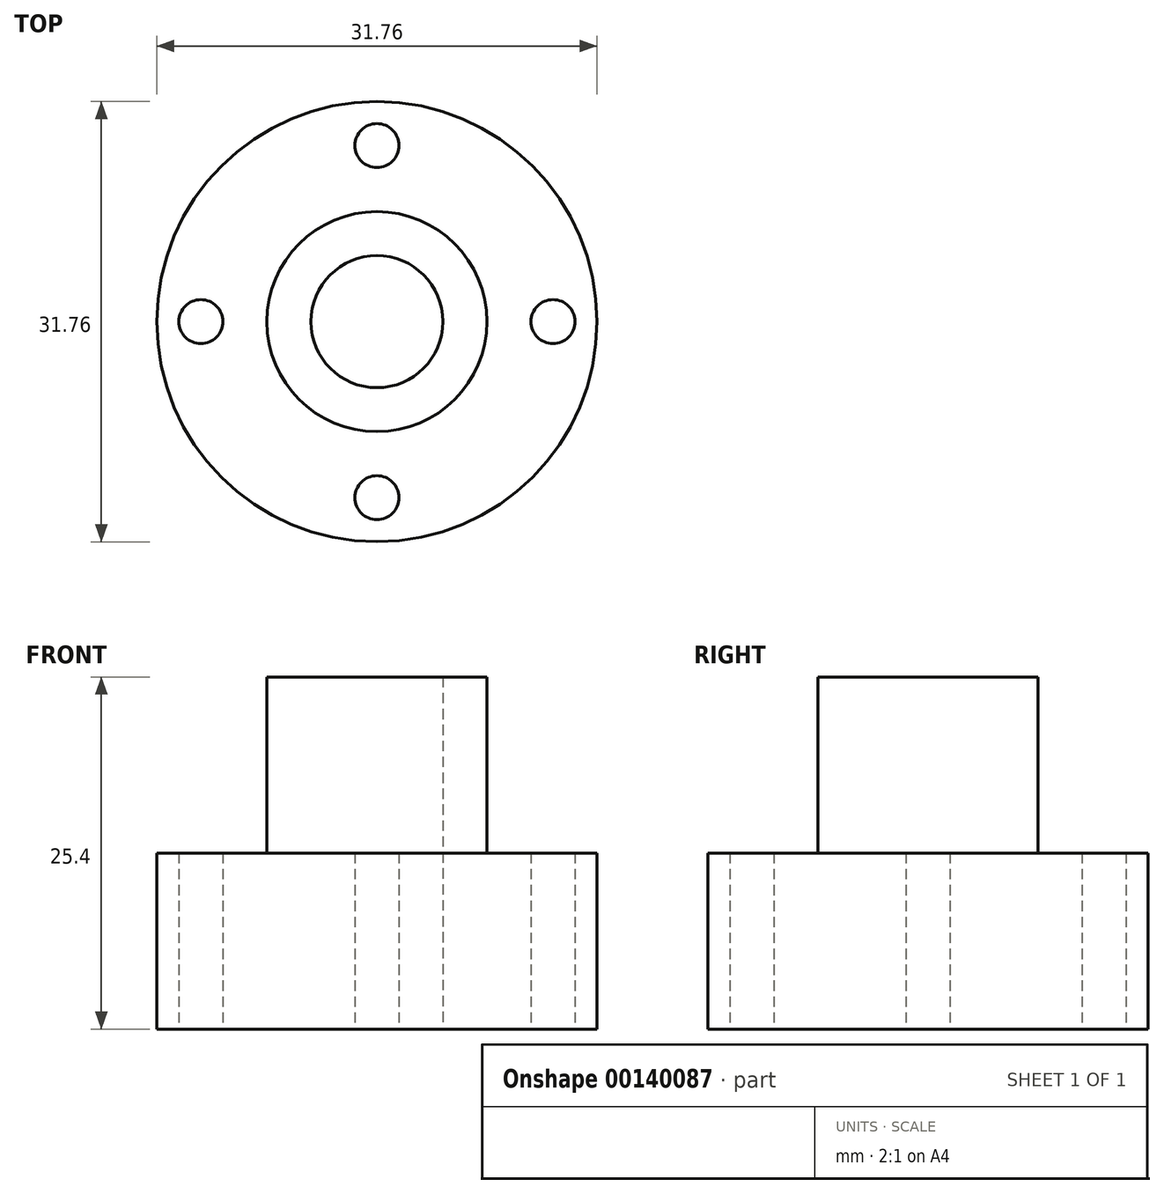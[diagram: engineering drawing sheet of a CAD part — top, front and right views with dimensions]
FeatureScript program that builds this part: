
annotation { "Feature Type Name" : "Feature", "Feature Type Description" : "" }
export const myFeature = defineFeature(function(context is Context, id is Id, definition is map)
    precondition{}
    {
        {
            var Q0;
            Q0=qCreatedBy(makeId("Top.planeOp"),FACE);
            var sketch = newSketch(context, id + "F0", { "sketchPlane" : qUnion([Q0])});
            skCircle(sketch, "E0", {"center": v(0, 0) * mm, "radius": 15.88 * mm});
            skSolve(sketch);
        }
        {
            var Q0;
            Q0 = qSketchRegion(id + "F0", true);
            extrude(context, id + "F1", {"entities" : qUnion([Q0]), "depth" : 12.7 * mm});
        }
        {
            var Q0;
            Q0=qCreatedBy(makeId("Top.planeOp"),FACE);
            var sketch = newSketch(context, id + "F2", { "sketchPlane" : qUnion([Q0])});
            skCircle(sketch, "E1", {"center": v(0, 0) * mm, "radius": 7.94 * mm});
            skSolve(sketch);
        }
        {
            var Q0;
            Q0 = qSketchRegion(id + "F2", true);
            extrude(context, id + "F3", {"entities" : qUnion([Q0]), "operationType" : NewBodyOperationType.ADD, "depth" : 25.4 * mm});
        }
        {
            var Q0;
            Q0=qCreatedBy(makeId("Top.planeOp"),FACE);
            var sketch = newSketch(context, id + "F4", { "sketchPlane" : qUnion([Q0])});
            skCircle(sketch, "E2", {"center": v(0, 0) * mm, "radius": 4.76 * mm});
            skSolve(sketch);
        }
        {
            var Q0;
            Q0 = qSketchRegion(id + "F4", true);
            extrude(context, id + "F5", {"entities" : qUnion([Q0]), "operationType" : NewBodyOperationType.REMOVE, "depth" : 25.4 * mm});
        }
        {
            var Q0;
            Q0=qCreatedBy(makeId("Top.planeOp"),FACE);
            var sketch = newSketch(context, id + "F6", { "sketchPlane" : qUnion([Q0])});
            skCircle(sketch, "E3", {"center": v(0, 0) * mm, "radius": 12.7 * mm, "construction": true});
            skCircle(sketch, "E4", {"center": v(0, 12.7) * mm, "radius": 1.59 * mm});
            skCircle(sketch, "E5", {"center": v(12.7, 0) * mm, "radius": 1.59 * mm});
            skCircle(sketch, "E6", {"center": v(-12.7, 0) * mm, "radius": 1.59 * mm});
            skCircle(sketch, "E7", {"center": v(0, -12.7) * mm, "radius": 1.59 * mm});
            skSolve(sketch);
        }
        {
            var Q0;
            Q0 = qSketchRegion(id + "F6", true);
            extrude(context, id + "F7", {"entities" : qUnion([Q0]), "operationType" : NewBodyOperationType.REMOVE, "depth" : 12.7 * mm});
        }
    });
